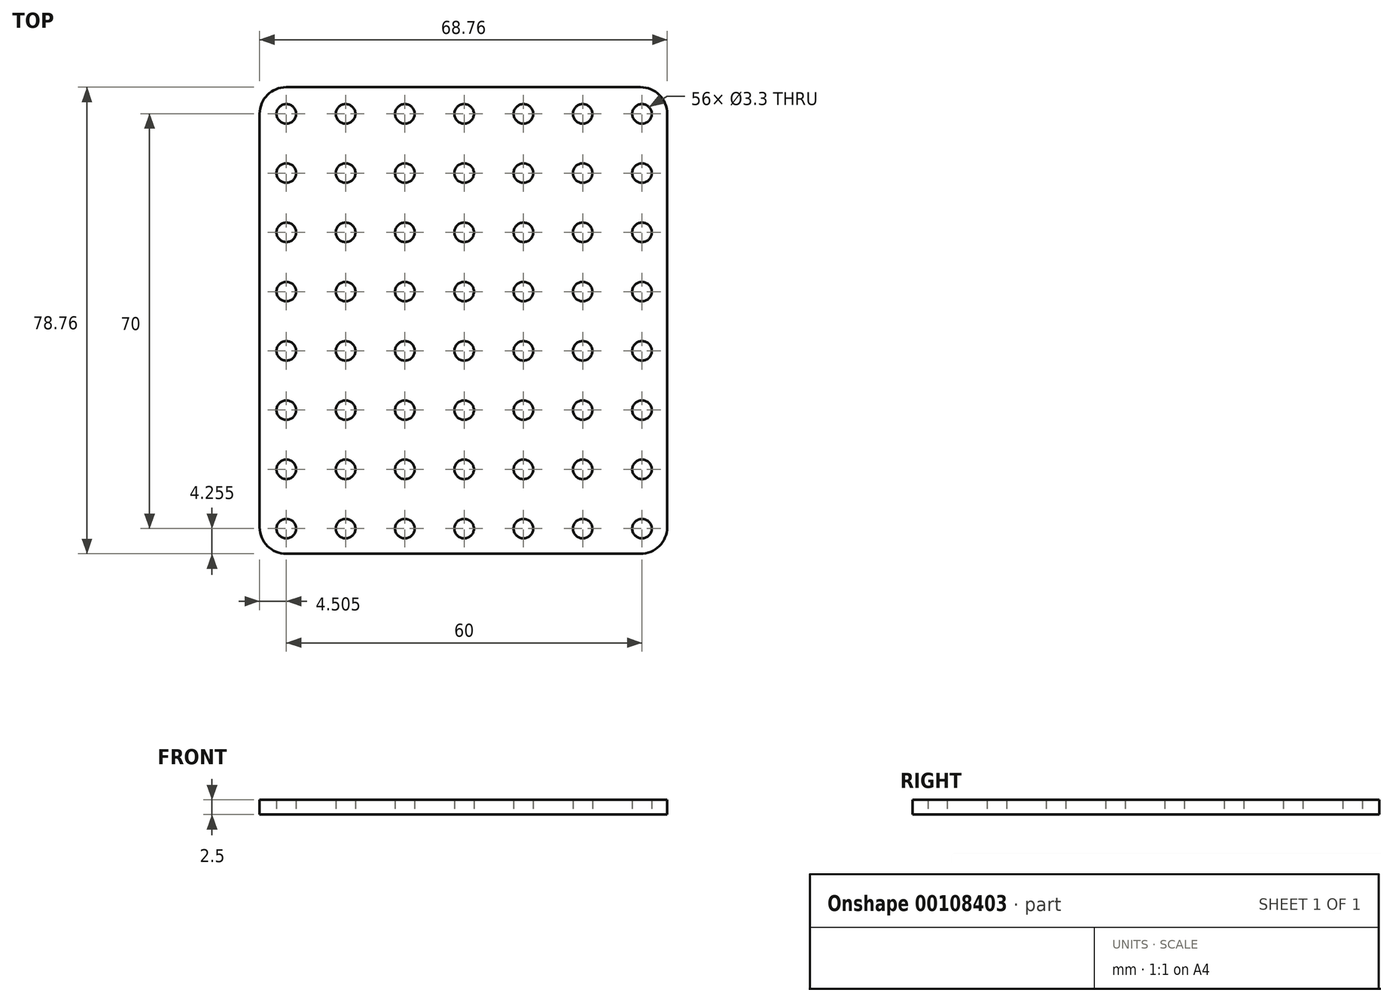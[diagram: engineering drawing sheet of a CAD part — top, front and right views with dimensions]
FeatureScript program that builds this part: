
annotation { "Feature Type Name" : "Feature", "Feature Type Description" : "" }
export const myFeature = defineFeature(function(context is Context, id is Id, definition is map)
    precondition{}
    {
        {
            var Q0;
            Q0=qCreatedBy(makeId("Top.planeOp"),FACE);
            var sketch = newSketch(context, id + "F0", { "sketchPlane" : qUnion([Q0])});
            skLineSegment(sketch, "E0.bottom", {"start": v(-34.37, 39.38) * mm, "end": v(34.38, 39.38) * mm});
            skLineSegment(sketch, "E0.top", {"start": v(-34.38, -39.38) * mm, "end": v(34.37, -39.38) * mm});
            skLineSegment(sketch, "E0.left", {"start": v(-34.37, 39.38) * mm, "end": v(-34.38, -39.38) * mm});
            skLineSegment(sketch, "E0.right", {"start": v(34.38, 39.38) * mm, "end": v(34.37, -39.38) * mm});
            skPoint(sketch, "E0.middle", {"position": v(0, 0) * mm});
            skLineSegment(sketch, "E1", {"start": v(-34.37, 34.88) * mm, "end": v(-29.87, 34.88) * mm, "construction": true});
            skLineSegment(sketch, "E2", {"start": v(-29.88, 34.88) * mm, "end": v(-29.88, 39.38) * mm, "construction": true});
            skCircle(sketch, "E3", {"center": v(-29.87, 34.88) * mm, "radius": 1.65 * mm});
            skCircle(sketch, "E4.0.1.0", {"center": v(-29.87, 24.88) * mm, "radius": 1.65 * mm});
            skCircle(sketch, "E4.0.2.0", {"center": v(-29.87, 14.88) * mm, "radius": 1.65 * mm});
            skCircle(sketch, "E4.0.3.0", {"center": v(-29.87, 4.87) * mm, "radius": 1.65 * mm});
            skCircle(sketch, "E4.0.4.0", {"center": v(-29.87, -5.13) * mm, "radius": 1.65 * mm});
            skCircle(sketch, "E4.0.5.0", {"center": v(-29.87, -15.13) * mm, "radius": 1.65 * mm});
            skCircle(sketch, "E4.0.6.0", {"center": v(-29.87, -25.13) * mm, "radius": 1.65 * mm});
            skCircle(sketch, "E4.0.7.0", {"center": v(-29.87, -35.12) * mm, "radius": 1.65 * mm});
            skCircle(sketch, "E4.1.0.0", {"center": v(-19.87, 34.88) * mm, "radius": 1.65 * mm});
            skCircle(sketch, "E4.1.1.0", {"center": v(-19.87, 24.88) * mm, "radius": 1.65 * mm});
            skCircle(sketch, "E4.1.2.0", {"center": v(-19.87, 14.88) * mm, "radius": 1.65 * mm});
            skCircle(sketch, "E4.1.3.0", {"center": v(-19.87, 4.87) * mm, "radius": 1.65 * mm});
            skCircle(sketch, "E4.1.4.0", {"center": v(-19.87, -5.13) * mm, "radius": 1.65 * mm});
            skCircle(sketch, "E4.1.5.0", {"center": v(-19.87, -15.13) * mm, "radius": 1.65 * mm});
            skCircle(sketch, "E4.1.6.0", {"center": v(-19.87, -25.13) * mm, "radius": 1.65 * mm});
            skCircle(sketch, "E4.1.7.0", {"center": v(-19.87, -35.12) * mm, "radius": 1.65 * mm});
            skCircle(sketch, "E4.2.0.0", {"center": v(-9.87, 34.88) * mm, "radius": 1.65 * mm});
            skCircle(sketch, "E4.2.1.0", {"center": v(-9.87, 24.88) * mm, "radius": 1.65 * mm});
            skCircle(sketch, "E4.2.2.0", {"center": v(-9.87, 14.88) * mm, "radius": 1.65 * mm});
            skCircle(sketch, "E4.2.3.0", {"center": v(-9.87, 4.87) * mm, "radius": 1.65 * mm});
            skCircle(sketch, "E4.2.4.0", {"center": v(-9.87, -5.13) * mm, "radius": 1.65 * mm});
            skCircle(sketch, "E4.2.5.0", {"center": v(-9.87, -15.13) * mm, "radius": 1.65 * mm});
            skCircle(sketch, "E4.2.6.0", {"center": v(-9.87, -25.13) * mm, "radius": 1.65 * mm});
            skCircle(sketch, "E4.2.7.0", {"center": v(-9.87, -35.12) * mm, "radius": 1.65 * mm});
            skCircle(sketch, "E4.3.0.0", {"center": v(0.13, 34.88) * mm, "radius": 1.65 * mm});
            skCircle(sketch, "E4.3.1.0", {"center": v(0.13, 24.88) * mm, "radius": 1.65 * mm});
            skCircle(sketch, "E4.3.2.0", {"center": v(0.13, 14.88) * mm, "radius": 1.65 * mm});
            skCircle(sketch, "E4.3.3.0", {"center": v(0.13, 4.87) * mm, "radius": 1.65 * mm});
            skCircle(sketch, "E4.3.4.0", {"center": v(0.13, -5.13) * mm, "radius": 1.65 * mm});
            skCircle(sketch, "E4.3.5.0", {"center": v(0.13, -15.13) * mm, "radius": 1.65 * mm});
            skCircle(sketch, "E4.3.6.0", {"center": v(0.13, -25.13) * mm, "radius": 1.65 * mm});
            skCircle(sketch, "E4.3.7.0", {"center": v(0.13, -35.12) * mm, "radius": 1.65 * mm});
            skCircle(sketch, "E4.4.0.0", {"center": v(10.12, 34.88) * mm, "radius": 1.65 * mm});
            skCircle(sketch, "E4.4.1.0", {"center": v(10.12, 24.88) * mm, "radius": 1.65 * mm});
            skCircle(sketch, "E4.4.2.0", {"center": v(10.12, 14.88) * mm, "radius": 1.65 * mm});
            skCircle(sketch, "E4.4.3.0", {"center": v(10.12, 4.87) * mm, "radius": 1.65 * mm});
            skCircle(sketch, "E4.4.4.0", {"center": v(10.12, -5.13) * mm, "radius": 1.65 * mm});
            skCircle(sketch, "E4.4.5.0", {"center": v(10.12, -15.13) * mm, "radius": 1.65 * mm});
            skCircle(sketch, "E4.4.6.0", {"center": v(10.12, -25.13) * mm, "radius": 1.65 * mm});
            skCircle(sketch, "E4.4.7.0", {"center": v(10.12, -35.12) * mm, "radius": 1.65 * mm});
            skCircle(sketch, "E4.5.0.0", {"center": v(20.12, 34.88) * mm, "radius": 1.65 * mm});
            skCircle(sketch, "E4.5.1.0", {"center": v(20.12, 24.88) * mm, "radius": 1.65 * mm});
            skCircle(sketch, "E4.5.2.0", {"center": v(20.12, 14.88) * mm, "radius": 1.65 * mm});
            skCircle(sketch, "E4.5.3.0", {"center": v(20.12, 4.87) * mm, "radius": 1.65 * mm});
            skCircle(sketch, "E4.5.4.0", {"center": v(20.12, -5.13) * mm, "radius": 1.65 * mm});
            skCircle(sketch, "E4.5.5.0", {"center": v(20.12, -15.13) * mm, "radius": 1.65 * mm});
            skCircle(sketch, "E4.5.6.0", {"center": v(20.12, -25.13) * mm, "radius": 1.65 * mm});
            skCircle(sketch, "E4.5.7.0", {"center": v(20.12, -35.12) * mm, "radius": 1.65 * mm});
            skCircle(sketch, "E4.6.0.0", {"center": v(30.12, 34.88) * mm, "radius": 1.65 * mm});
            skCircle(sketch, "E4.6.1.0", {"center": v(30.12, 24.88) * mm, "radius": 1.65 * mm});
            skCircle(sketch, "E4.6.2.0", {"center": v(30.12, 14.88) * mm, "radius": 1.65 * mm});
            skCircle(sketch, "E4.6.3.0", {"center": v(30.12, 4.87) * mm, "radius": 1.65 * mm});
            skCircle(sketch, "E4.6.4.0", {"center": v(30.12, -5.13) * mm, "radius": 1.65 * mm});
            skCircle(sketch, "E4.6.5.0", {"center": v(30.12, -15.13) * mm, "radius": 1.65 * mm});
            skCircle(sketch, "E4.6.6.0", {"center": v(30.12, -25.13) * mm, "radius": 1.65 * mm});
            skCircle(sketch, "E4.6.7.0", {"center": v(30.12, -35.12) * mm, "radius": 1.65 * mm});
            skLineSegment(sketch, "E4.direction1", {"start": v(-29.87, 34.88) * mm, "end": v(-19.87, 34.88) * mm, "construction": true});
            skLineSegment(sketch, "E4.direction2", {"start": v(-29.87, 34.88) * mm, "end": v(-29.87, 24.88) * mm, "construction": true});
            skSolve(sketch);
        }
        {
            var Q0;
            Q0 = qSketchRegion(id + "F0", true);
            extrude(context, id + "F1", {"entities" : qUnion([Q0]), "depth" : 2.5 * mm});
        }
        {
            var Q0;
            Q0=makeQuery(id+"F1.opExtrude","SWEPT_EDGE",EDGE,{"disambiguationData":[OSD([sQuery(id+"F0.wireOp",EDGE,"E0.bottom"),sQuery(id+"F0.wireOp",EDGE,"E0.right")])]});
            var Q1;
            Q1=makeQuery(id+"F1.opExtrude","SWEPT_EDGE",EDGE,{"disambiguationData":[OSD([sQuery(id+"F0.wireOp",EDGE,"E0.top"),sQuery(id+"F0.wireOp",EDGE,"E0.right")])]});
            var Q2;
            Q2=makeQuery(id+"F1.opExtrude","SWEPT_EDGE",EDGE,{"disambiguationData":[OSD([sQuery(id+"F0.wireOp",EDGE,"E0.bottom"),sQuery(id+"F0.wireOp",EDGE,"E0.left")])]});
            var Q3;
            Q3=makeQuery(id+"F1.opExtrude","SWEPT_EDGE",EDGE,{"disambiguationData":[OSD([sQuery(id+"F0.wireOp",EDGE,"E0.top"),sQuery(id+"F0.wireOp",EDGE,"E0.left")])]});
            fillet(context, id + "F2", {"entities" : qUnion([Q0, Q1, Q2, Q3]), "radius" : 4.5 * mm, "tangentPropagation" : true, "allowEdgeOverflow" : false});
        }
    });
